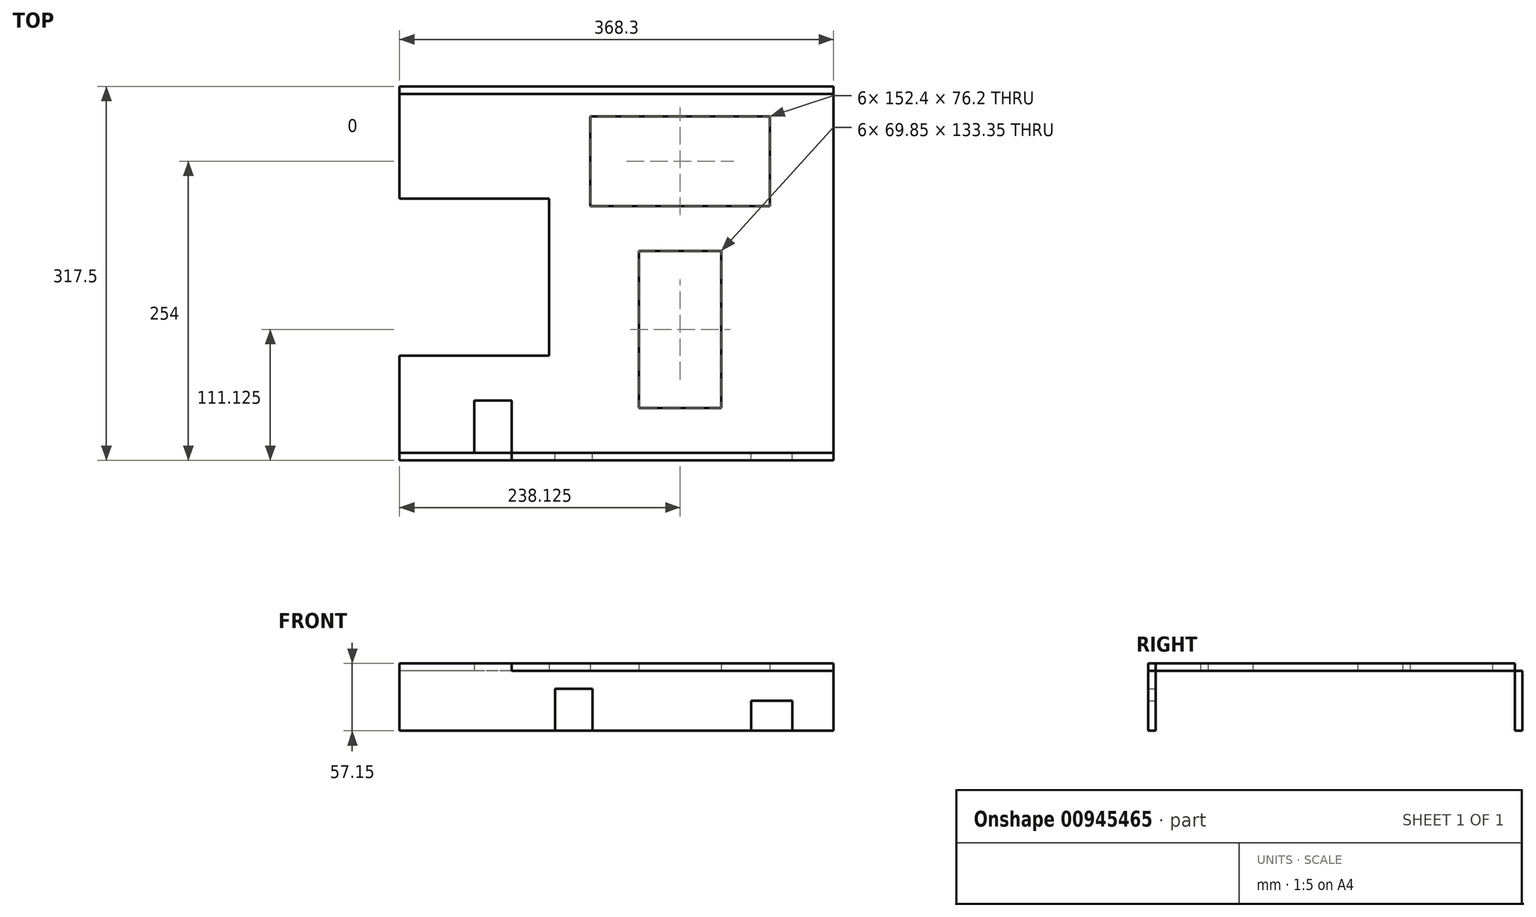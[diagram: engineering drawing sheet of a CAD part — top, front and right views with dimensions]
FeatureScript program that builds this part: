
annotation { "Feature Type Name" : "Feature", "Feature Type Description" : "" }
export const myFeature = defineFeature(function(context is Context, id is Id, definition is map)
    precondition{}
    {
        {
            var Q0;
            Q0=qCreatedBy(makeId("Top.planeOp"),FACE);
            var sketch = newSketch(context, id + "F0", { "sketchPlane" : qUnion([Q0])});
            skLineSegment(sketch, "E0", {"start": v(-95.25, 19.05) * mm, "end": v(273.05, 19.05) * mm});
            skLineSegment(sketch, "E1", {"start": v(273.05, 19.05) * mm, "end": v(273.05, -285.75) * mm});
            skLineSegment(sketch, "E2", {"start": v(273.05, -285.75) * mm, "end": v(0, -285.75) * mm});
            skLineSegment(sketch, "E3", {"start": v(0, -285.75) * mm, "end": v(0, -241.3) * mm});
            skLineSegment(sketch, "E4", {"start": v(0, -241.3) * mm, "end": v(-31.75, -241.3) * mm});
            skLineSegment(sketch, "E5", {"start": v(-31.75, -241.3) * mm, "end": v(-31.75, -285.75) * mm});
            skLineSegment(sketch, "E6", {"start": v(-31.75, -285.75) * mm, "end": v(-95.25, -285.75) * mm});
            skLineSegment(sketch, "E7", {"start": v(-95.25, -285.75) * mm, "end": v(-95.25, -203.2) * mm});
            skLineSegment(sketch, "E8", {"start": v(-95.25, -203.2) * mm, "end": v(31.75, -203.2) * mm});
            skLineSegment(sketch, "E9", {"start": v(31.75, -203.2) * mm, "end": v(31.75, -69.85) * mm});
            skLineSegment(sketch, "E10", {"start": v(31.75, -69.85) * mm, "end": v(-95.25, -69.85) * mm});
            skLineSegment(sketch, "E11", {"start": v(-95.25, -69.85) * mm, "end": v(-95.25, 19.05) * mm});
            skLineSegment(sketch, "E12.bottom", {"start": v(66.67, 0) * mm, "end": v(219.07, 0) * mm});
            skLineSegment(sketch, "E12.top", {"start": v(66.67, -76.2) * mm, "end": v(219.07, -76.2) * mm});
            skLineSegment(sketch, "E12.left", {"start": v(66.67, 0) * mm, "end": v(66.67, -76.2) * mm});
            skLineSegment(sketch, "E12.right", {"start": v(219.07, 0) * mm, "end": v(219.07, -76.2) * mm});
            skLineSegment(sketch, "E13.bottom", {"start": v(107.95, -114.3) * mm, "end": v(177.8, -114.3) * mm});
            skLineSegment(sketch, "E13.top", {"start": v(107.95, -247.65) * mm, "end": v(177.8, -247.65) * mm});
            skLineSegment(sketch, "E13.left", {"start": v(107.95, -114.3) * mm, "end": v(107.95, -247.65) * mm});
            skLineSegment(sketch, "E13.right", {"start": v(177.8, -114.3) * mm, "end": v(177.8, -247.65) * mm});
            skSolve(sketch);
        }
        {
            var Q0;
            Q0=makeQuery(id+"F0.imprint","IMPRINT",FACE,{"disambiguationData":[TD([[makeQuery(id+"F0.imprint","IMPRINT",EDGE,{"derivedFrom":sQuery(id+"F0.wireOp",EDGE,"E0")}),-1.0]])]});
            extrude(context, id + "F1", {"entities" : qUnion([Q0]), "depth" : 6.35 * mm, "offsetDistance" : 25.4 * mm});
        }
        {
            var Q0;
            Q0=makeQuery(id+"F1.opExtrude","SWEPT_FACE",FACE,{"disambiguationData":[OSD([sQuery(id+"F0.wireOp",EDGE,"E0")])]});
            var sketch = newSketch(context, id + "F2", { "sketchPlane" : qUnion([Q0])});
            skLineSegment(sketch, "E14", {"start": v(-273.05, 6.35) * mm, "end": v(95.25, 6.35) * mm});
            skLineSegment(sketch, "E15", {"start": v(95.25, 6.35) * mm, "end": v(95.25, -50.8) * mm});
            skLineSegment(sketch, "E16", {"start": v(95.25, -50.8) * mm, "end": v(-273.05, -50.8) * mm});
            skLineSegment(sketch, "E17", {"start": v(-273.05, -50.8) * mm, "end": v(-273.05, 6.35) * mm});
            skSolve(sketch);
        }
        {
            var Q0;
            {var subQ2=sQuery(id+"F2.wireOp",EDGE,"E16");Q0=makeQuery(id+"F2.imprint","IMPRINT",FACE,{"disambiguationData":[TD([[makeQuery(id+"F2.imprint","IMPRINT",EDGE,{"derivedFrom":subQ2}),-1.0]])]});}
            extrude(context, id + "F3", {"entities" : qUnion([Q0]), "depth" : 6.35 * mm, "offsetDistance" : 25.4 * mm});
        }
        {
            var Q0;
            Q0=makeQuery(id+"F1.opExtrude","SWEPT_FACE",FACE,{"disambiguationData":[OSD([sQuery(id+"F0.wireOp",EDGE,"E2")])]});
            var sketch = newSketch(context, id + "F4", { "sketchPlane" : qUnion([Q0])});
            skLineSegment(sketch, "E18", {"start": v(273.05, 6.35) * mm, "end": v(-95.25, 6.35) * mm});
            skLineSegment(sketch, "E19", {"start": v(-95.25, 6.35) * mm, "end": v(-95.25, -50.8) * mm});
            skLineSegment(sketch, "E20", {"start": v(273.05, 6.35) * mm, "end": v(273.05, -50.8) * mm});
            skLineSegment(sketch, "E21", {"start": v(273.05, -50.8) * mm, "end": v(238.12, -50.8) * mm});
            skLineSegment(sketch, "E22", {"start": v(238.12, -50.8) * mm, "end": v(238.12, -25.4) * mm});
            skLineSegment(sketch, "E23", {"start": v(238.12, -25.4) * mm, "end": v(203.2, -25.4) * mm});
            skLineSegment(sketch, "E24", {"start": v(203.2, -25.4) * mm, "end": v(203.2, -50.8) * mm});
            skLineSegment(sketch, "E25", {"start": v(203.2, -50.8) * mm, "end": v(68.58, -50.8) * mm});
            skLineSegment(sketch, "E26", {"start": v(68.58, -50.8) * mm, "end": v(68.58, -15.24) * mm});
            skLineSegment(sketch, "E27", {"start": v(68.58, -15.24) * mm, "end": v(36.83, -15.24) * mm});
            skLineSegment(sketch, "E28", {"start": v(36.83, -15.24) * mm, "end": v(36.83, -50.8) * mm});
            skLineSegment(sketch, "E29", {"start": v(36.83, -50.8) * mm, "end": v(-95.25, -50.8) * mm});
            skLineSegment(sketch, "E30", {"start": v(-95.25, 6.35) * mm, "end": v(273.05, 6.35) * mm});
            skSolve(sketch);
        }
        {
            var Q0;
            {var subQ3=sQuery(id+"F4.wireOp",EDGE,"E19");Q0=makeQuery(id+"F4.imprint","IMPRINT",FACE,{"disambiguationData":[TD([[makeQuery(id+"F4.imprint","IMPRINT",EDGE,{"derivedFrom":subQ3}),1.0]])]});}
            extrude(context, id + "F5", {"entities" : qUnion([Q0]), "depth" : 6.35 * mm, "offsetDistance" : 25.4 * mm});
        }
    });
